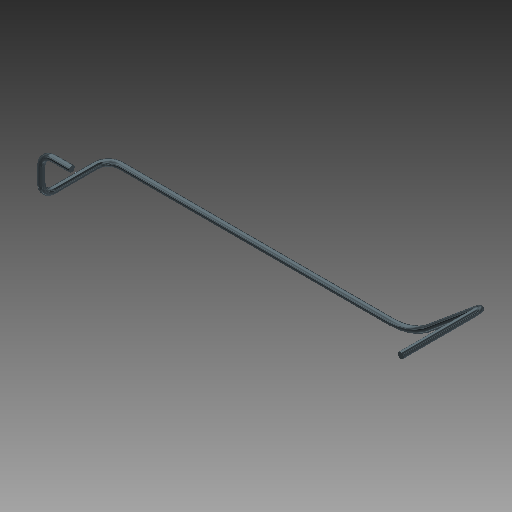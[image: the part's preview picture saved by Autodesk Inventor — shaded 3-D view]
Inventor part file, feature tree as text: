
AUTODESK INVENTOR PART (.ipt)
format: ipt  version: 2019 (Build 230136000, 136)  size: 116,736 bytes
history: native  units: mm
features: sketch x5, plane x4, sweep x1
ambient origin geometry x8: Origin, YZ Plane, XZ Plane, XY Plane, X Axis, Y Axis, Z Axis, Center Point
bodies: Solid1 (feature_tree)
feature tree (10):
  plane  "Work Plane1"
  plane  "Work Plane2"
  plane  "Work Plane3"
  sketch  "Sketch2"  dims[d0=-70.0mm d1=-50.0mm d2=-310.0mm d3=250.0mm]
  sketch  "Sketch3"  dims[d4=50.0mm]
  plane  "Work Plane4"
  sketch  "Sketch4"  dims[d5=55.0mm]
  sweep  "Sweep1"
  sketch  "3D Sketch1"
  sketch  "Sketch5"  dims[d6=32.5mm d7=25.0mm d8=10.0mm d9=10.0mm d10=10.0mm d11=10.0mm d12=50.0mm d13=5.0mm d14=0.0mm d15=0.0mm]
